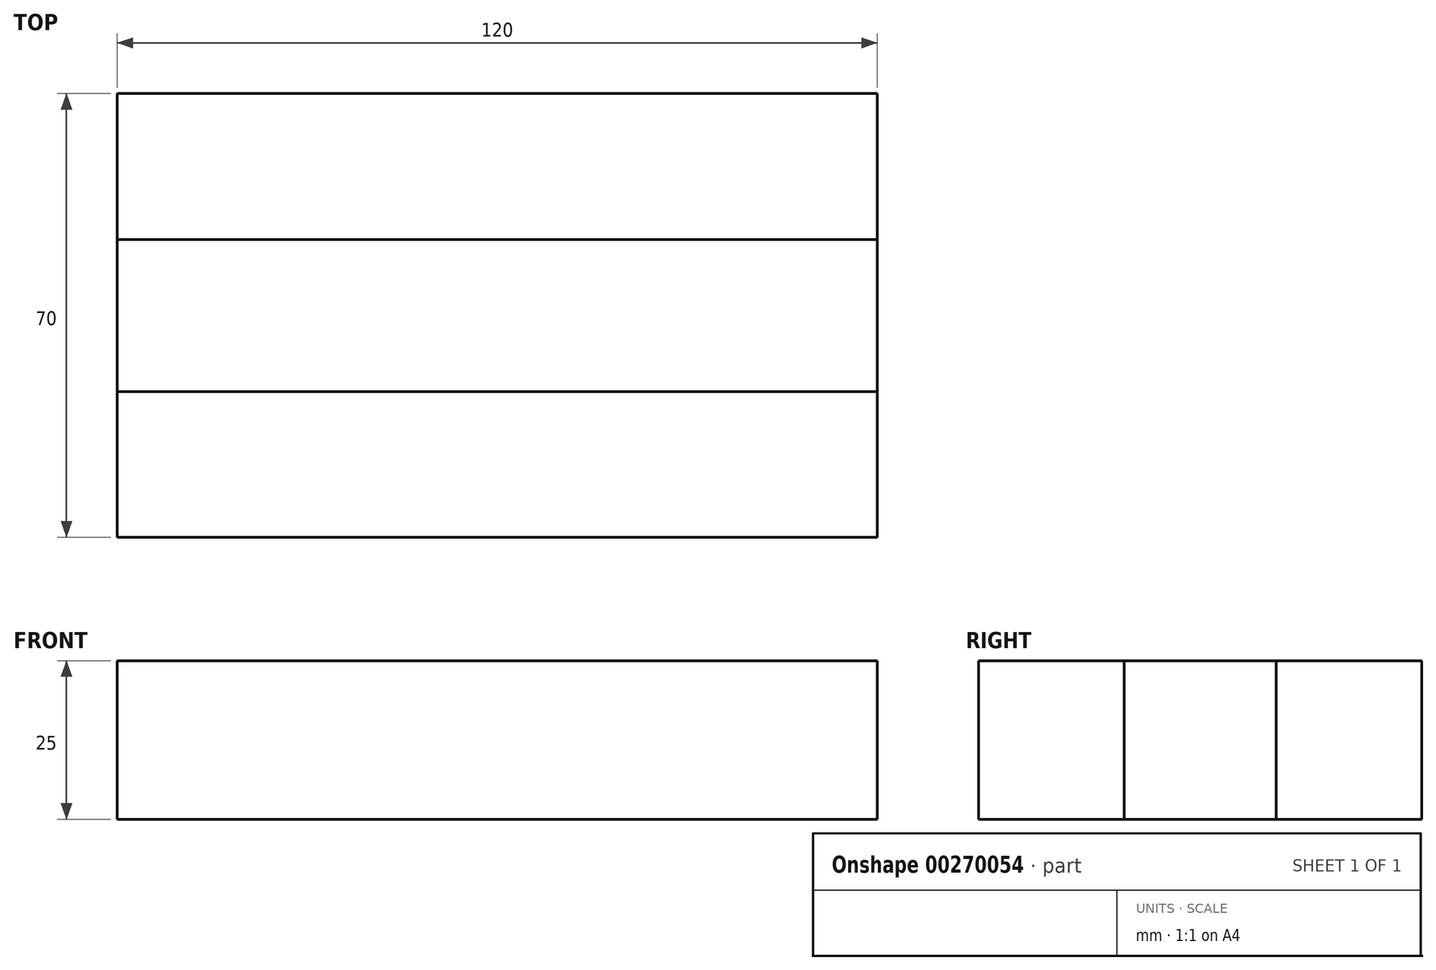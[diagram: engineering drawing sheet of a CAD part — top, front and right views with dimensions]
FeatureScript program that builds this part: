
annotation { "Feature Type Name" : "Feature", "Feature Type Description" : "" }
export const myFeature = defineFeature(function(context is Context, id is Id, definition is map)
    precondition{}
    {
        {
            var Q0;
            Q0=qCreatedBy(makeId("Top.planeOp"),FACE);
            var sketch = newSketch(context, id + "F0", { "sketchPlane" : qUnion([Q0])});
            skLineSegment(sketch, "E0.bottom", {"start": v(-56.76, 23) * mm, "end": v(63.24, 23) * mm});
            skLineSegment(sketch, "E0.top", {"start": v(-56.76, -47) * mm, "end": v(63.24, -47) * mm});
            skLineSegment(sketch, "E0.left", {"start": v(-56.76, 23) * mm, "end": v(-56.76, -47) * mm});
            skLineSegment(sketch, "E0.right", {"start": v(63.24, 23) * mm, "end": v(63.24, -47) * mm});
            skPoint(sketch, "E1.end.orphan", {"position": v(63.24, -12) * mm});
            skPoint(sketch, "E1.start.orphan", {"position": v(-56.76, -12) * mm});
            skLineSegment(sketch, "E2", {"start": v(-56.76, -24) * mm, "end": v(63.24, -24) * mm});
            skLineSegment(sketch, "E3", {"start": v(-56.76, 0) * mm, "end": v(63.24, 0) * mm});
            skSolve(sketch);
        }
        {
            var Q0;
            {var subQ0=sQuery(id+"F0.wireOp",EDGE,"E0.top");Q0=makeQuery(id+"F0.imprint","IMPRINT",FACE,{"disambiguationData":[TD([[makeQuery(id+"F0.imprint","IMPRINT",EDGE,{"derivedFrom":subQ0}),1.0]])]});}
            var Q1;
            {var subQ0=sQuery(id+"F0.wireOp",EDGE,"E0.bottom");Q1=makeQuery(id+"F0.imprint","IMPRINT",FACE,{"disambiguationData":[TD([[makeQuery(id+"F0.imprint","IMPRINT",EDGE,{"derivedFrom":subQ0}),-1.0]])]});}
            extrude(context, id + "F1", {"entities" : qUnion([Q0, Q1]), "depth" : 25 * mm});
        }
        {
            var Q0;
            {var subQ0=sQuery(id+"F0.wireOp",EDGE,"E2");Q0=makeQuery(id+"F0.imprint","IMPRINT",FACE,{"disambiguationData":[TD([[makeQuery(id+"F0.imprint","IMPRINT",EDGE,{"derivedFrom":subQ0}),1.0]])]});}
            extrude(context, id + "F2", {"entities" : qUnion([Q0]), "depth" : 25 * mm});
        }
    });
